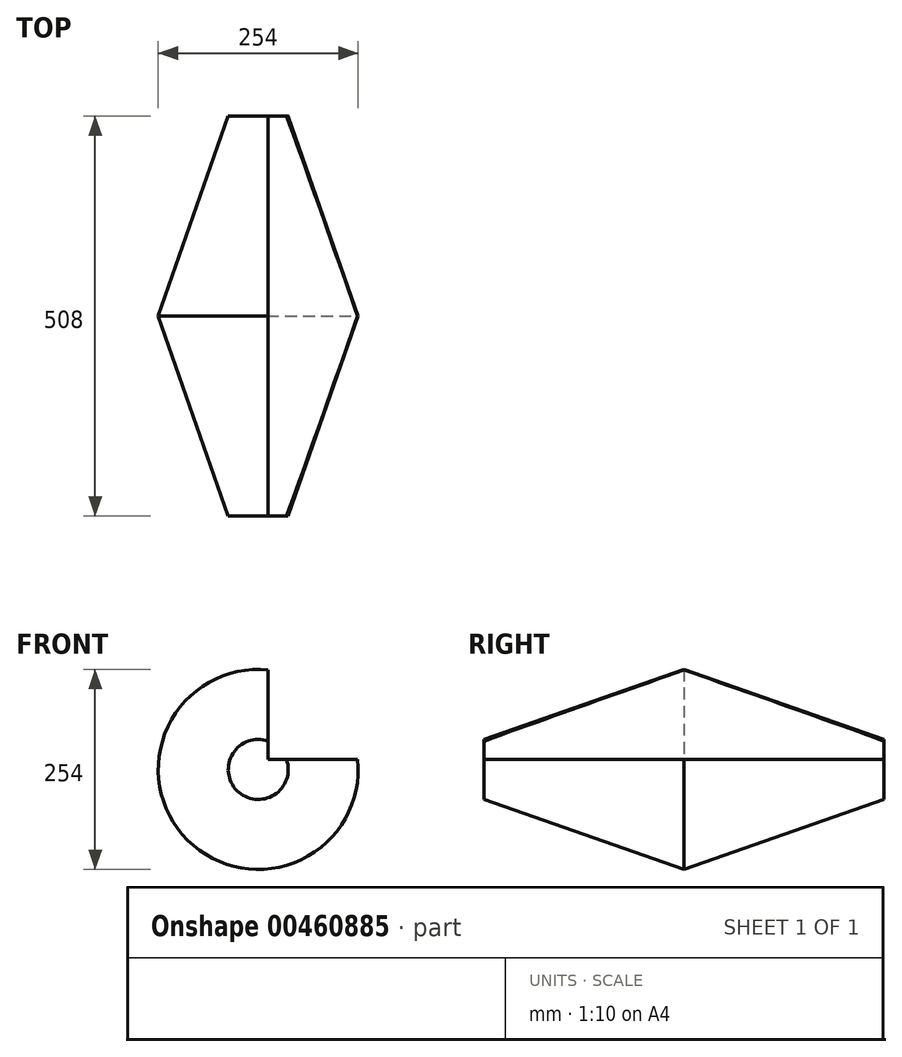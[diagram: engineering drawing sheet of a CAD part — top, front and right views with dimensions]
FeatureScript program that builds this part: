
annotation { "Feature Type Name" : "Feature", "Feature Type Description" : "" }
export const myFeature = defineFeature(function(context is Context, id is Id, definition is map)
    precondition{}
    {
        {
            var Q0;
            Q0=qCreatedBy(makeId("Front.planeOp"),FACE);
            var sketch = newSketch(context, id + "F0", { "sketchPlane" : qUnion([Q0])});
            skCircle(sketch, "E0", {"center": v(0, 0) * mm, "radius": 127 * mm});
            skSolve(sketch);
        }
        {
            var Q0;
            Q0=qCreatedBy(makeId("Front.planeOp"),FACE);
            cPlane(context, id + "F1", {"entities" : qUnion([Q0]), "cplaneType" : CPlaneType.OFFSET, "offset" : 254 * mm, "width" : 152.4 * mm, "height" : 152.4 * mm});
        }
        {
            var Q0;
            Q0=qCreatedBy(id+"F1.planeOp",FACE);
            var sketch = newSketch(context, id + "F2", { "sketchPlane" : qUnion([Q0])});
            skCircle(sketch, "E1", {"center": v(0, 0) * mm, "radius": 38.1 * mm});
            skSolve(sketch);
        }
        {
            var Q0;
            Q0 = qSketchRegion(id + "F2", true);
            var Q1;
            Q1 = qSketchRegion(id + "F0", true);
            loft(context, id + "F3", {"sheetProfilesArray" : [{ "sheetProfileEntities" : qUnion([Q0]) }, { "sheetProfileEntities" : qUnion([Q1]) }]});
        }
        {
            var Q0;
            Q0=makeQuery(id+"F3.opLoft","CAP_FACE",FACE,{"disambiguationData":[OSD([makeQuery(id+"F2.imprint","IMPRINT",FACE,{"disambiguationData":[TD([[makeQuery(id+"F2.imprint","IMPRINT",EDGE,{"derivedFrom":sQuery(id+"F2.wireOp",EDGE,"E1")}),1.0]])]})])],"isStart":true});
            var sketch = newSketch(context, id + "F4", { "sketchPlane" : qUnion([Q0])});
            skLineSegment(sketch, "E2", {"start": v(0, 62.33) * mm, "end": v(0, -68.3) * mm, "construction": true});
            skLineSegment(sketch, "E3", {"start": v(-72.8, 0) * mm, "end": v(73.14, 0) * mm, "construction": true});
            skLineSegment(sketch, "E4", {"start": v(12.7, 49.19) * mm, "end": v(12.7, 12.7) * mm});
            skLineSegment(sketch, "E5", {"start": v(12.7, 12.7) * mm, "end": v(49.19, 12.7) * mm});
            skArc(sketch, "E6", {"start": v(12.7, 49.19) * mm, "mid": v(35.92, 35.92) * mm, "end": v(49.19, 12.7) * mm});
            skSolve(sketch);
        }
        {
            var Q0;
            Q0=makeQuery(id+"F3.opLoft","CAP_FACE",FACE,{"disambiguationData":[OSD([makeQuery(id+"F0.imprint","IMPRINT",FACE,{"disambiguationData":[TD([[makeQuery(id+"F0.imprint","IMPRINT",EDGE,{"derivedFrom":sQuery(id+"F0.wireOp",EDGE,"E0")}),1.0]])]})])],"isStart":true});
            var sketch = newSketch(context, id + "F5", { "sketchPlane" : qUnion([Q0])});
            skLineSegment(sketch, "E7", {"start": v(0, 154.23) * mm, "end": v(0, -164.21) * mm, "construction": true});
            skLineSegment(sketch, "E8", {"start": v(156.24, 0) * mm, "end": v(-158.68, 0) * mm, "construction": true});
            skLineSegment(sketch, "E9", {"start": v(-12.7, 156.12) * mm, "end": v(-12.7, 12.7) * mm});
            skLineSegment(sketch, "E10", {"start": v(-12.7, 12.7) * mm, "end": v(-156.12, 12.7) * mm});
            skArc(sketch, "E11", {"start": v(-12.7, 156.12) * mm, "mid": v(-110.76, 110.76) * mm, "end": v(-156.12, 12.7) * mm});
            skSolve(sketch);
        }
        {
            var Q1;
            Q1 = qSketchRegion(id + "F4", true);
            var Q2;
            Q2 = qSketchRegion(id + "F5", true);
            loft(context, id + "F6", {"operationType" : NewBodyOperationType.REMOVE, "sheetProfilesArray" : [{ "sheetProfileEntities" : qUnion([Q1]) }, { "sheetProfileEntities" : qUnion([Q2]) }]});
        }
        {
            var Q0;
            Q0=makeQuery(id+"F3.opLoft","SWEPT_BODY",BODY,{"disambiguationData":[OSD([makeQuery(id+"F0.imprint","IMPRINT",FACE,{"disambiguationData":[TD([[makeQuery(id+"F0.imprint","IMPRINT",EDGE,{"derivedFrom":sQuery(id+"F0.wireOp",EDGE,"E0")}),1.0]])]}),makeQuery(id+"F2.imprint","IMPRINT",FACE,{"disambiguationData":[TD([[makeQuery(id+"F2.imprint","IMPRINT",EDGE,{"derivedFrom":sQuery(id+"F2.wireOp",EDGE,"E1")}),1.0]])]})])]});
            var Q1;
            Q1=makeQuery(id+"F3.opLoft","CAP_FACE",FACE,{"disambiguationData":[OSD([makeQuery(id+"F0.imprint","IMPRINT",FACE,{"disambiguationData":[TD([[makeQuery(id+"F0.imprint","IMPRINT",EDGE,{"derivedFrom":sQuery(id+"F0.wireOp",EDGE,"E0")}),1.0]])]})])],"isStart":true});
            mirror(context, id + "F7", {"operationType" : NewBodyOperationType.ADD, "entities" : qUnion([Q0]), "mirrorPlane" : qUnion([Q1])});
        }
    });
